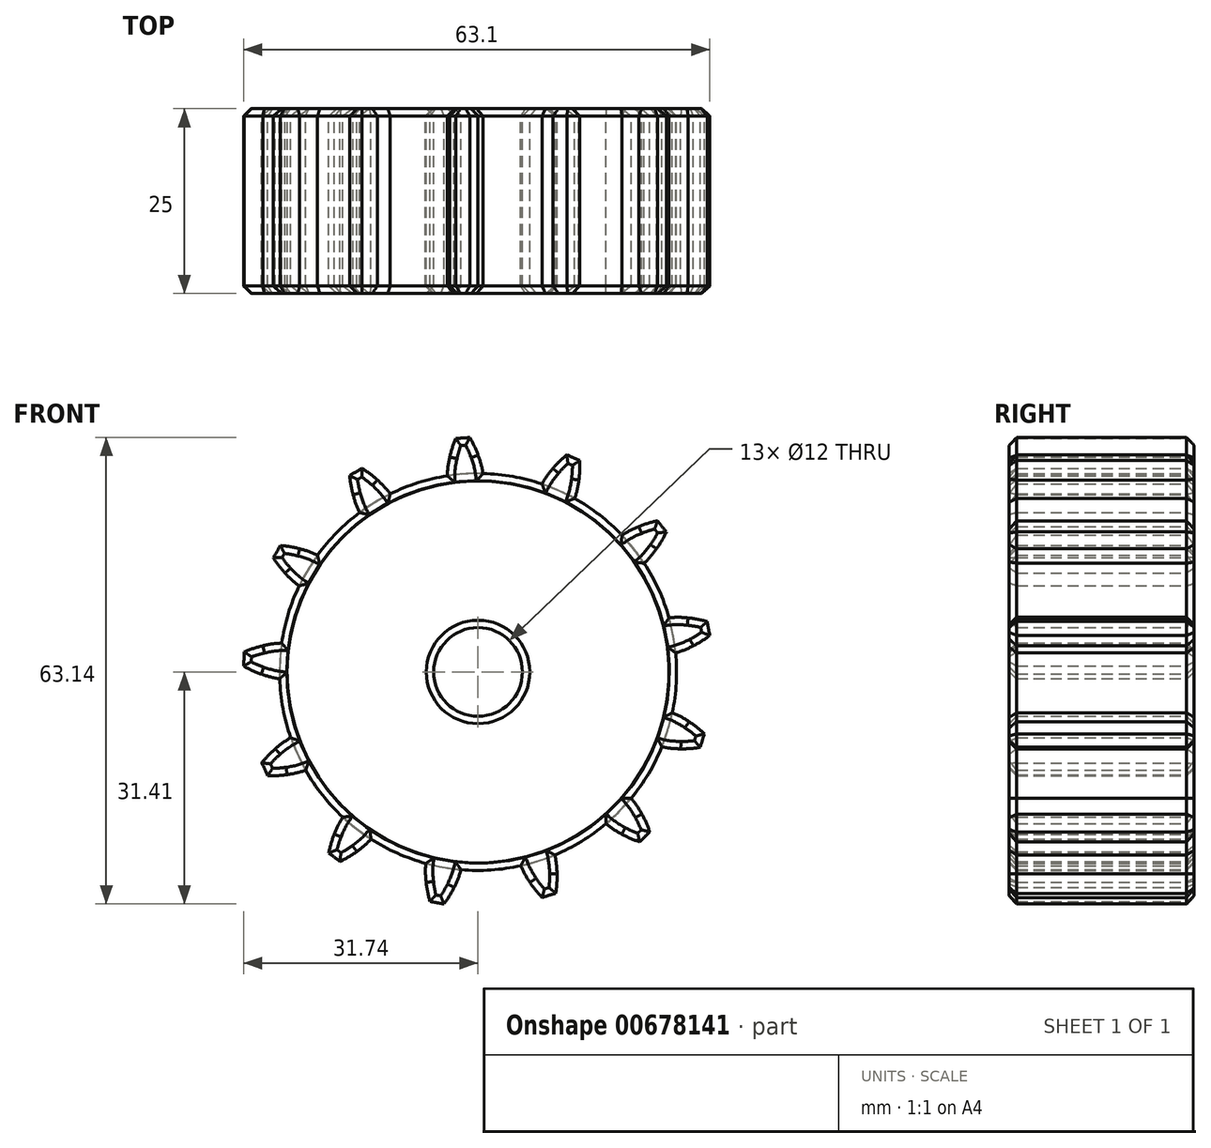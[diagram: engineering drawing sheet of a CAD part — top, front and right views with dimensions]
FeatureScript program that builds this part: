
annotation { "Feature Type Name" : "Feature", "Feature Type Description" : "" }
export const myFeature = defineFeature(function(context is Context, id is Id, definition is map)
    precondition{}
    {
        {
            var Q0;
            Q0=qCreatedBy(makeId("Front.planeOp"),FACE);
            var sketch = newSketch(context, id + "F0", { "sketchPlane" : qUnion([Q0])});
            skCircle(sketch, "E0", {"center": v(0, 0) * mm, "radius": 26.86 * mm});
            skCircle(sketch, "E1", {"center": v(0, 0) * mm, "radius": 29.34 * mm, "construction": true});
            skCircle(sketch, "E2", {"center": v(0, 0) * mm, "radius": 31.75 * mm, "construction": true});
            skLineSegment(sketch, "E3", {"start": v(0, 0) * mm, "end": v(0, 86.26) * mm, "construction": true});
            skLineSegment(sketch, "E4", {"start": v(0, 0) * mm, "end": v(-5.65, 86.26) * mm, "construction": true});
            skLineSegment(sketch, "E5", {"start": v(0, 29.34) * mm, "end": v(-58.15, 29.34) * mm, "construction": true});
            skLineSegment(sketch, "E6", {"start": v(0, 29.34) * mm, "end": v(-58.26, 8.13) * mm, "construction": true});
            skCircle(sketch, "E7", {"center": v(0, 0) * mm, "radius": 27.57 * mm, "construction": true});
            skCircle(sketch, "E8", {"center": v(0, 29.34) * mm, "radius": 14.6 * mm, "construction": true});
            skCircle(sketch, "E9", {"center": v(-13.72, 24.34) * mm, "radius": 14.6 * mm, "construction": true});
            skArc(sketch, "E10", {"start": v(0, 29.34) * mm, "mid": v(-0.5, 30.56) * mm, "end": v(-1.13, 31.73) * mm});
            skArc(sketch, "E11", {"start": v(0.66, 26.85) * mm, "mid": v(0.4, 28.11) * mm, "end": v(0, 29.34) * mm});
            skArc(sketch, "E12.MirrorCS", {"start": v(-3.83, 29.09) * mm, "mid": v(-3.49, 30.37) * mm, "end": v(-3.03, 31.6) * mm});
            skArc(sketch, "E13.MirrorCS", {"start": v(-4.16, 26.54) * mm, "mid": v(-4.07, 27.82) * mm, "end": v(-3.83, 29.09) * mm});
            skArc(sketch, "E14", {"start": v(-3.03, 31.6) * mm, "mid": v(-2.07, 31.65) * mm, "end": v(-1.13, 31.73) * mm});
            skCircle(sketch, "E15", {"center": v(0, 0) * mm, "radius": 6 * mm});
            skSolve(sketch);
        }
        {
            var Q0;
            {var subQ0=sQuery(id+"F0.wireOp",EDGE,"E0");var subQ1=makeQuery(id+"F0.imprint","INTERSECT",VERTEX,{"derivedFrom":[subQ0,sQuery(id+"F0.wireOp",EDGE,"E11")]});Q0=makeQuery(id+"F0.imprint","IMPRINT",FACE,{"disambiguationData":[TD([[makeQuery(id+"F0.imprint","IMPRINT",EDGE,{"disambiguationData":[TD([[subQ1,-1.0]])],"derivedFrom":subQ0}),1.0]])]});}
            var Q1;
            {var subQ0=sQuery(id+"F0.wireOp",EDGE,"E11");Q1=makeQuery(id+"F0.imprint","IMPRINT",FACE,{"disambiguationData":[TD([[makeQuery(id+"F0.imprint","IMPRINT",EDGE,{"derivedFrom":subQ0}),1.0]])]});}
            var Q2;
            Q2=makeQuery(id+"F0.imprint","IMPRINT",FACE,{"disambiguationData":[TD([[makeQuery(id+"F0.imprint","IMPRINT",EDGE,{"derivedFrom":sQuery(id+"F0.wireOp",EDGE,"vKZVkNDW-wY9Q-CPGG-XcqL-Y2yGn7BmyWEc")}),1.0]])]});
            extrude(context, id + "F1", {"entities" : qUnion([Q0, Q1, Q2]), "depth" : 25 * mm, "offsetDistance" : 25 * mm});
        }
        {
            var Q0;
            Q0=makeQuery(id+"F1.opExtrude","SWEPT_BODY",BODY,{"disambiguationData":[OSD([sQuery(id+"F0.wireOp",EDGE,"E0"),sQuery(id+"F0.wireOp",EDGE,"E10"),sQuery(id+"F0.wireOp",EDGE,"E11"),sQuery(id+"F0.wireOp",EDGE,"E12.MirrorCS"),sQuery(id+"F0.wireOp",EDGE,"E13.MirrorCS"),sQuery(id+"F0.wireOp",EDGE,"E14")])]});
            var Q1;
            Q1=makeQuery(id+"F1.opExtrude","SWEPT_FACE",FACE,{"disambiguationData":[OSD([sQuery(id+"F0.wireOp",EDGE,"E0")])]});
            circularPattern(context, id + "F2", {"entities" : qUnion([Q0]), "axis" : qUnion([Q1]), "angle" : 360 * degree, "instanceCount" : 13, "equalSpace" : true});
        }
        {
            var Q0;
            {var subQ0=makeQuery(id+"F1.opExtrude","CAP_FACE",FACE,{"disambiguationData":[OSD([sQuery(id+"F0.wireOp",EDGE,"E0"),sQuery(id+"F0.wireOp",EDGE,"E10"),sQuery(id+"F0.wireOp",EDGE,"E11"),sQuery(id+"F0.wireOp",EDGE,"E12.MirrorCS"),sQuery(id+"F0.wireOp",EDGE,"E13.MirrorCS"),sQuery(id+"F0.wireOp",EDGE,"E14"),sQuery(id+"F0.wireOp",EDGE,"vKZVkNDW-wY9Q-CPGG-XcqL-Y2yGn7BmyWEc")])],"isStart":false});Q0=makeQuery(id+"FXCni8fr6ZgspXB_1.boolean.opBoolean","MERGE",FACE,{"derivedFrom":[subQ0,makeQuery(id+"F2.opPattern","COPY",FACE,{"derivedFrom":subQ0,"instanceName":"1"}),makeQuery(id+"F2.opPattern","COPY",FACE,{"derivedFrom":subQ0,"instanceName":"2"}),makeQuery(id+"F2.opPattern","COPY",FACE,{"derivedFrom":subQ0,"instanceName":"3"}),makeQuery(id+"F2.opPattern","COPY",FACE,{"derivedFrom":subQ0,"instanceName":"4"}),makeQuery(id+"F2.opPattern","COPY",FACE,{"derivedFrom":subQ0,"instanceName":"5"}),makeQuery(id+"F2.opPattern","COPY",FACE,{"derivedFrom":subQ0,"instanceName":"6"}),makeQuery(id+"F2.opPattern","COPY",FACE,{"derivedFrom":subQ0,"instanceName":"7"}),makeQuery(id+"F2.opPattern","COPY",FACE,{"derivedFrom":subQ0,"instanceName":"8"}),makeQuery(id+"F2.opPattern","COPY",FACE,{"derivedFrom":subQ0,"instanceName":"9"}),makeQuery(id+"F2.opPattern","COPY",FACE,{"derivedFrom":subQ0,"instanceName":"10"}),makeQuery(id+"F2.opPattern","COPY",FACE,{"derivedFrom":subQ0,"instanceName":"11"}),makeQuery(id+"F2.opPattern","COPY",FACE,{"derivedFrom":subQ0,"instanceName":"12"}),makeQuery(id+"F2.opPattern","COPY",FACE,{"derivedFrom":subQ0,"instanceName":"13"}),makeQuery(id+"F2.opPattern","COPY",FACE,{"derivedFrom":subQ0,"instanceName":"14"}),makeQuery(id+"F2.opPattern","COPY",FACE,{"derivedFrom":subQ0,"instanceName":"15"}),makeQuery(id+"F2.opPattern","COPY",FACE,{"derivedFrom":subQ0,"instanceName":"16"}),makeQuery(id+"F2.opPattern","COPY",FACE,{"derivedFrom":subQ0,"instanceName":"17"}),makeQuery(id+"F2.opPattern","COPY",FACE,{"derivedFrom":subQ0,"instanceName":"18"}),makeQuery(id+"F2.opPattern","COPY",FACE,{"derivedFrom":subQ0,"instanceName":"19"}),makeQuery(id+"F2.opPattern","COPY",FACE,{"derivedFrom":subQ0,"instanceName":"20"}),makeQuery(id+"F2.opPattern","COPY",FACE,{"derivedFrom":subQ0,"instanceName":"21"}),makeQuery(id+"F2.opPattern","COPY",FACE,{"derivedFrom":subQ0,"instanceName":"22"}),makeQuery(id+"F2.opPattern","COPY",FACE,{"derivedFrom":subQ0,"instanceName":"23"}),makeQuery(id+"F2.opPattern","COPY",FACE,{"derivedFrom":subQ0,"instanceName":"24"}),makeQuery(id+"F2.opPattern","COPY",FACE,{"derivedFrom":subQ0,"instanceName":"25"})]});}
            chamfer(context, id + "F3", {"entities" : qUnion([Q0]), "width" : 1 * mm, "tangentPropagation" : true});
        }
        {
            var Q0;
            {var subQ0=sQuery(id+"F0.wireOp",EDGE,"vKZVkNDW-wY9Q-CPGG-XcqL-Y2yGn7BmyWEc");var subQ1=makeQuery(id+"F1.opExtrude","CAP_FACE",FACE,{"disambiguationData":[OSD([sQuery(id+"F0.wireOp",EDGE,"E0"),sQuery(id+"F0.wireOp",EDGE,"E10"),sQuery(id+"F0.wireOp",EDGE,"E11"),sQuery(id+"F0.wireOp",EDGE,"E12.MirrorCS"),sQuery(id+"F0.wireOp",EDGE,"E13.MirrorCS"),sQuery(id+"F0.wireOp",EDGE,"E14"),subQ0])],"isStart":true});Q0=makeQuery(id+"FXCni8fr6ZgspXB_1.boolean.opBoolean","MERGE",FACE,{"derivedFrom":[subQ1,makeQuery(id+"F2.opPattern","COPY",FACE,{"derivedFrom":subQ1,"instanceName":"1"}),makeQuery(id+"F2.opPattern","COPY",FACE,{"derivedFrom":subQ1,"instanceName":"2"}),makeQuery(id+"F2.opPattern","COPY",FACE,{"derivedFrom":subQ1,"instanceName":"3"}),makeQuery(id+"F2.opPattern","COPY",FACE,{"derivedFrom":subQ1,"instanceName":"4"}),makeQuery(id+"F2.opPattern","COPY",FACE,{"derivedFrom":subQ1,"instanceName":"5"}),makeQuery(id+"F2.opPattern","COPY",FACE,{"derivedFrom":subQ1,"instanceName":"6"}),makeQuery(id+"F2.opPattern","COPY",FACE,{"derivedFrom":subQ1,"instanceName":"7"}),makeQuery(id+"F2.opPattern","COPY",FACE,{"derivedFrom":subQ1,"instanceName":"8"}),makeQuery(id+"F2.opPattern","COPY",FACE,{"derivedFrom":subQ1,"instanceName":"9"}),makeQuery(id+"F2.opPattern","COPY",FACE,{"derivedFrom":subQ1,"instanceName":"10"}),makeQuery(id+"F2.opPattern","COPY",FACE,{"derivedFrom":subQ1,"instanceName":"11"}),makeQuery(id+"F2.opPattern","COPY",FACE,{"derivedFrom":subQ1,"instanceName":"12"}),makeQuery(id+"F2.opPattern","COPY",FACE,{"derivedFrom":subQ1,"instanceName":"13"}),makeQuery(id+"F2.opPattern","COPY",FACE,{"derivedFrom":subQ1,"instanceName":"14"}),makeQuery(id+"F2.opPattern","COPY",FACE,{"derivedFrom":subQ1,"instanceName":"15"}),makeQuery(id+"F2.opPattern","COPY",FACE,{"derivedFrom":subQ1,"instanceName":"16"}),makeQuery(id+"F2.opPattern","COPY",FACE,{"derivedFrom":subQ1,"instanceName":"17"}),makeQuery(id+"F2.opPattern","COPY",FACE,{"derivedFrom":subQ1,"instanceName":"18"}),makeQuery(id+"F2.opPattern","COPY",FACE,{"derivedFrom":subQ1,"instanceName":"19"}),makeQuery(id+"F2.opPattern","COPY",FACE,{"derivedFrom":subQ1,"instanceName":"20"}),makeQuery(id+"F2.opPattern","COPY",FACE,{"derivedFrom":subQ1,"instanceName":"21"}),makeQuery(id+"F2.opPattern","COPY",FACE,{"derivedFrom":subQ1,"instanceName":"22"}),makeQuery(id+"F2.opPattern","COPY",FACE,{"derivedFrom":subQ1,"instanceName":"23"}),makeQuery(id+"F2.opPattern","COPY",FACE,{"derivedFrom":subQ1,"instanceName":"24"}),makeQuery(id+"F2.opPattern","COPY",FACE,{"derivedFrom":subQ1,"instanceName":"25"}),makeQuery(id+"FXCni8fr6ZgspXB_1.opExtrude","CAP_FACE",FACE,{"disambiguationData":[OSD([subQ0,sQuery(id+"F0.wireOp",EDGE,"pL8NEk07-toPv-Y8c3-0pR4-N81YuIIMofPY"),sQuery(id+"F0.wireOp",EDGE,"rYt4CUGk-5RMG-IGir-F2Id-Z486pLvJte1b"),sQuery(id+"F0.wireOp",EDGE,"gwXLB29B-QVIw-rg2I-bR0U-6sGXIXwzs039"),sQuery(id+"F0.wireOp",EDGE,"UOqMCenV-wbyt-e5UZ-am8R-yHaWSJiJpqQw")])],"isStart":true})]});}
            chamfer(context, id + "F4", {"entities" : qUnion([Q0]), "width" : 1 * mm, "tangentPropagation" : true});
        }
    });
